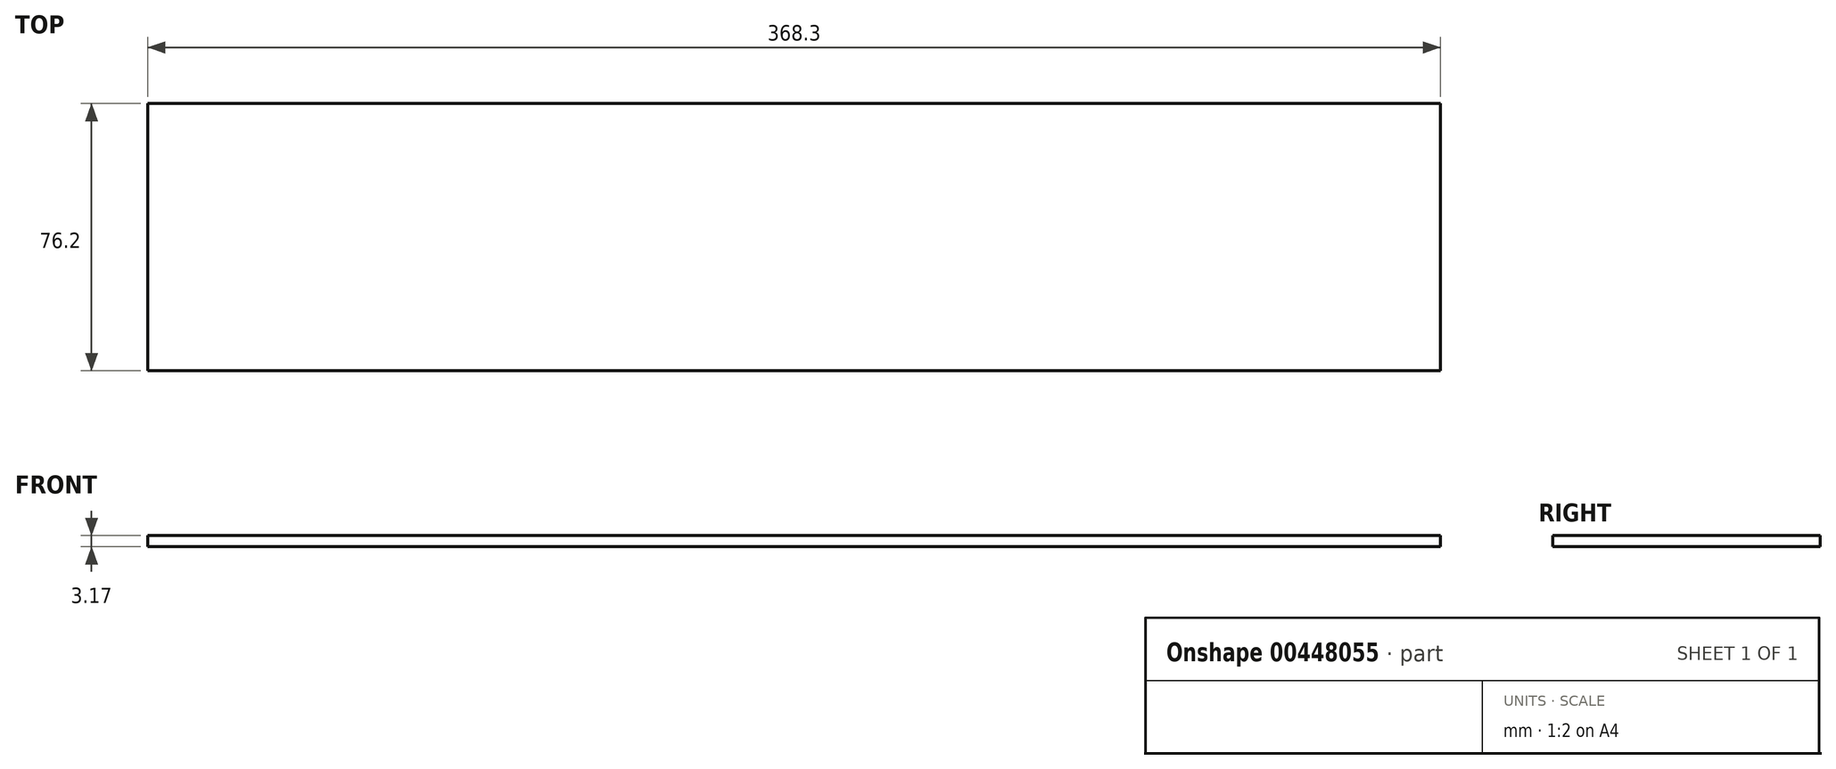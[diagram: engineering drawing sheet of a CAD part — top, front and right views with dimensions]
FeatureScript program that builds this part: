
annotation { "Feature Type Name" : "Feature", "Feature Type Description" : "" }
export const myFeature = defineFeature(function(context is Context, id is Id, definition is map)
    precondition{}
    {
        {
            var Q0;
            Q0=qCreatedBy(makeId("Top.planeOp"),FACE);
            var sketch = newSketch(context, id + "F0", { "sketchPlane" : qUnion([Q0])});
            skLineSegment(sketch, "E0.bottom", {"start": v(-184.15, 38.1) * mm, "end": v(184.15, 38.1) * mm});
            skLineSegment(sketch, "E0.top", {"start": v(-184.15, -38.1) * mm, "end": v(184.15, -38.1) * mm});
            skLineSegment(sketch, "E0.left", {"start": v(-184.15, 38.1) * mm, "end": v(-184.15, -38.1) * mm});
            skLineSegment(sketch, "E0.right", {"start": v(184.15, 38.1) * mm, "end": v(184.15, -38.1) * mm});
            skPoint(sketch, "E0.middle", {"position": v(0, 0) * mm});
            skSolve(sketch);
        }
        {
            var Q0;
            Q0=qSketchRegion(id+"F0",true);
            extrude(context, id + "F1", {"entities" : qUnion([Q0]), "depth" : 3.17 * mm});
        }
    });
